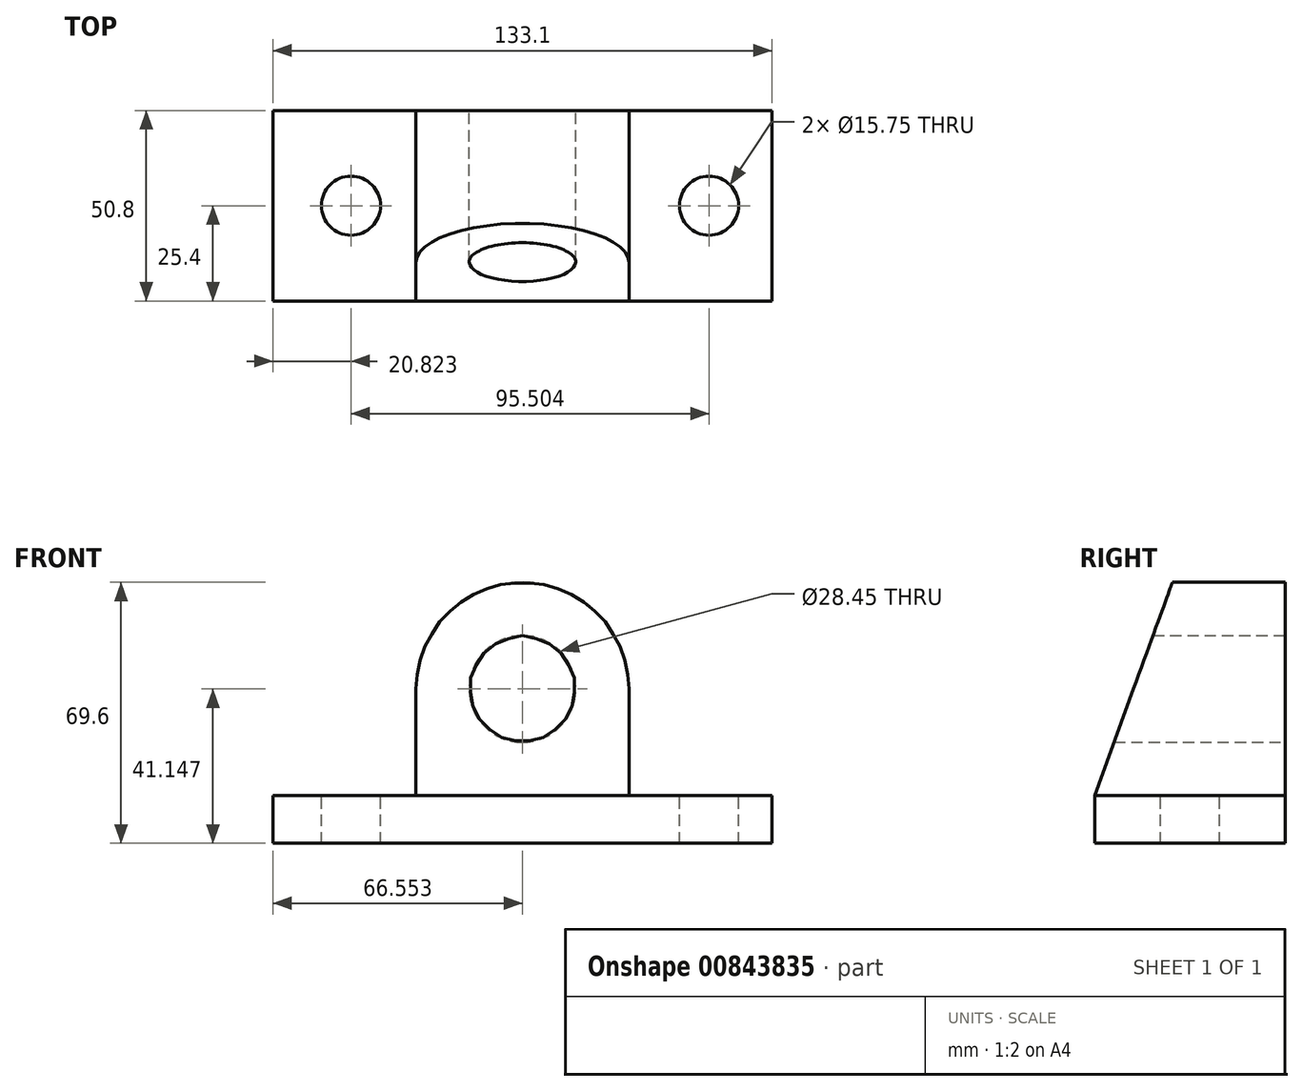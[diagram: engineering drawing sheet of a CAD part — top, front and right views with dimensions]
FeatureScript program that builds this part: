
annotation { "Feature Type Name" : "Feature", "Feature Type Description" : "" }
export const myFeature = defineFeature(function(context is Context, id is Id, definition is map)
    precondition{}
    {
        {
            var Q0;
            Q0=qCreatedBy(makeId("Front.planeOp"),FACE);
            var sketch = newSketch(context, id + "F0", { "sketchPlane" : qUnion([Q0])});
            skLineSegment(sketch, "E0.bottom", {"start": v(-70.7, 11.9) * mm, "end": v(62.4, 11.9) * mm});
            skLineSegment(sketch, "E0.top", {"start": v(-70.7, -0.8) * mm, "end": v(62.4, -0.8) * mm});
            skLineSegment(sketch, "E0.left", {"start": v(-70.7, 11.9) * mm, "end": v(-70.7, -0.8) * mm});
            skLineSegment(sketch, "E0.right", {"start": v(62.4, 11.9) * mm, "end": v(62.4, -0.8) * mm});
            skLineSegment(sketch, "E1.bottom", {"start": v(-32.6, 11.9) * mm, "end": v(24.3, 11.9) * mm});
            skLineSegment(sketch, "E1.left", {"start": v(-32.6, 11.9) * mm, "end": v(-32.6, 14.96) * mm});
            skLineSegment(sketch, "E1.right", {"start": v(24.3, 11.9) * mm, "end": v(24.3, 14.96) * mm});
            skLineSegment(sketch, "E2", {"start": v(-32.6, 14.96) * mm, "end": v(-32.6, 40.36) * mm});
            skLineSegment(sketch, "E3", {"start": v(24.3, 14.96) * mm, "end": v(24.3, 40.36) * mm});
            skArc(sketch, "E4", {"start": v(24.3, 40.36) * mm, "mid": v(-4.16, 68.8) * mm, "end": v(-32.6, 40.36) * mm});
            skCircle(sketch, "E5", {"center": v(-4.16, 40.36) * mm, "radius": 14.22 * mm});
            skSolve(sketch);
        }
        {
            var Q0;
            Q0 = qSketchRegion(id + "F0", true);
            extrude(context, id + "F1", {"entities" : qUnion([Q0]), "depth" : 50.8 * mm, "offsetDistance" : 25.4 * mm});
        }
        {
            var Q0;
            Q0=makeQuery(id+"F1.opExtrude","SWEPT_FACE",FACE,{"disambiguationData":[OSD([sQuery(id+"F0.wireOp",EDGE,"E1.right"),sQuery(id+"F0.wireOp",EDGE,"E3")])]});
            var sketch = newSketch(context, id + "F2", { "sketchPlane" : qUnion([Q0])});
            skLineSegment(sketch, "E6", {"start": v(-50.8, 11.9) * mm, "end": v(-28.74, 72.51) * mm});
            skLineSegment(sketch, "E7", {"start": v(-50.8, 11.9) * mm, "end": v(0, 11.9) * mm});
            skLineSegment(sketch, "E8", {"start": v(0, 11.9) * mm, "end": v(0, 72.51) * mm});
            skLineSegment(sketch, "E9", {"start": v(-50.8, 72.51) * mm, "end": v(-50.8, 11.9) * mm});
            skLineSegment(sketch, "E10", {"start": v(-50.8, 72.51) * mm, "end": v(0, 72.51) * mm});
            skLineSegment(sketch, "E11", {"start": v(0, 72.51) * mm, "end": v(0, 68.94) * mm});
            skLineSegment(sketch, "E12", {"start": v(-50.8, 68.8) * mm, "end": v(-50.8, 72.51) * mm});
            skLineSegment(sketch, "E13", {"start": v(-50.8, 68.8) * mm, "end": v(-28.74, 68.8) * mm});
            skLineSegment(sketch, "E14", {"start": v(-28.74, 72.51) * mm, "end": v(-28.74, 68.8) * mm});
            skSolve(sketch);
        }
        {
            var Q0;
            {var subQ0=sQuery(id+"F2.wireOp",EDGE,"E10");var subQ1=sQuery(id+"F2.wireOp",EDGE,"E6");var subQ2=makeQuery(id+"F2.imprint","INTERSECT",VERTEX,{"derivedFrom":[subQ1,subQ0]});Q0=makeQuery(id+"F2.imprint","IMPRINT",FACE,{"disambiguationData":[TD([[makeQuery(id+"F2.imprint","IMPRINT",EDGE,{"disambiguationData":[TD([[subQ2,1.0]])],"derivedFrom":subQ0}),-1.0]])]});}
            var Q1;
            {var subQ0=sQuery(id+"F2.wireOp",EDGE,"E9");var subQ1=sQuery(id+"F2.wireOp",EDGE,"E6");var subQ2=makeQuery(id+"F2.imprint","INTERSECT",VERTEX,{"derivedFrom":[subQ1,sQuery(id+"F2.wireOp",EDGE,"E7"),subQ0]});Q1=makeQuery(id+"F2.imprint","IMPRINT",FACE,{"disambiguationData":[TD([[makeQuery(id+"F2.imprint","IMPRINT",EDGE,{"disambiguationData":[TD([[subQ2,-1.0]])],"derivedFrom":subQ1}),1.0]])]});}
            var Q2;
            {var subQ0=sQuery(id+"F2.wireOp",EDGE,"E13");var subQ1=sQuery(id+"F2.wireOp",EDGE,"E6");var subQ2=makeQuery(id+"F2.imprint","INTERSECT",VERTEX,{"derivedFrom":[subQ1,subQ0]});Q2=makeQuery(id+"F2.imprint","IMPRINT",FACE,{"disambiguationData":[TD([[makeQuery(id+"F2.imprint","IMPRINT",EDGE,{"disambiguationData":[TD([[subQ2,1.0]])],"derivedFrom":subQ1}),1.0]])]});}
            extrude(context, id + "F3", {"entities" : qUnion([Q0, Q1, Q2]), "operationType" : NewBodyOperationType.REMOVE, "oppositeDirection" : true, "depth" : 177.8 * mm, "offsetDistance" : 25.4 * mm});
        }
        {
            var Q0;
            {var subQ0=sQuery(id+"F0.wireOp",EDGE,"E0.bottom");Q0=makeQuery(id+"F1.opExtrude","SWEPT_FACE",FACE,{"disambiguationData":[OSD([subQ0]),TDD([makeQuery(id+"F0.imprint","IMPRINT",EDGE,{"disambiguationData":[TD([[makeQuery(id+"F0.imprint","INTERSECT",VERTEX,{"derivedFrom":[subQ0,sQuery(id+"F0.wireOp",EDGE,"E0.left")]}),-1.0]])],"derivedFrom":subQ0})])]});}
            var sketch = newSketch(context, id + "F4", { "sketchPlane" : qUnion([Q0])});
            skCircle(sketch, "E15", {"center": v(-49.89, -25.4) * mm, "radius": 7.87 * mm});
            skCircle(sketch, "E16", {"center": v(45.62, -25.4) * mm, "radius": 7.87 * mm});
            skPoint(sketch, "E16.centerSnap0", {"position": v(-32.6, -25.4) * mm});
            skLineSegment(sketch, "E17", {"start": v(-2.63, -30.06) * mm, "end": v(-1.64, -30.06) * mm, "construction": true});
            skLineSegment(sketch, "E18", {"start": v(-1.64, -30.06) * mm, "end": v(-2.13, -30.06) * mm, "construction": true});
            skLineSegment(sketch, "E19", {"start": v(-2.13, -30.06) * mm, "end": v(-2.13, -21.47) * mm, "construction": true});
            skSolve(sketch);
        }
        {
            var Q0;
            Q0=makeQuery(id+"F4.imprint","IMPRINT",FACE,{"disambiguationData":[TD([[makeQuery(id+"F4.imprint","IMPRINT",EDGE,{"derivedFrom":sQuery(id+"F4.wireOp",EDGE,"E15")}),1.0]])]});
            var Q1;
            Q1=makeQuery(id+"F4.imprint","IMPRINT",FACE,{"disambiguationData":[TD([[makeQuery(id+"F4.imprint","IMPRINT",EDGE,{"derivedFrom":sQuery(id+"F4.wireOp",EDGE,"E16")}),1.0]])]});
            extrude(context, id + "F5", {"entities" : qUnion([Q0, Q1]), "operationType" : NewBodyOperationType.REMOVE, "oppositeDirection" : true, "depth" : 25.4 * mm, "offsetDistance" : 25.4 * mm});
        }
    });
